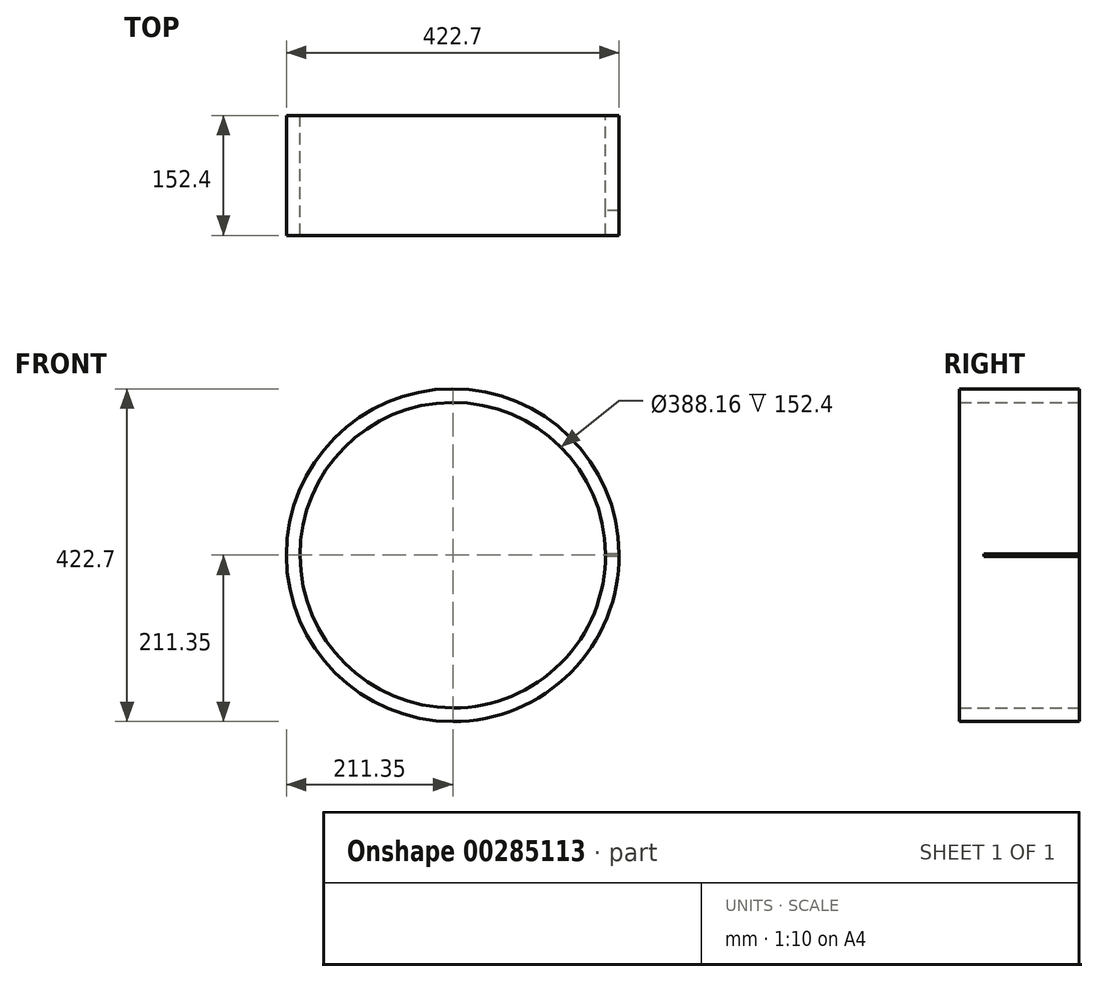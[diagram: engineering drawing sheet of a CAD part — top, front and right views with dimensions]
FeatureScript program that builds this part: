
annotation { "Feature Type Name" : "Feature", "Feature Type Description" : "" }
export const myFeature = defineFeature(function(context is Context, id is Id, definition is map)
    precondition{}
    {
        {
            var Q0;
            Q0=qCreatedBy(makeId("Front.planeOp"),FACE);
            var sketch = newSketch(context, id + "F0", { "sketchPlane" : qUnion([Q0])});
            skCircle(sketch, "E0", {"center": v(0, 0) * mm, "radius": 211.35 * mm});
            skCircle(sketch, "E1", {"center": v(0, 0) * mm, "radius": 194.08 * mm});
            skSolve(sketch);
        }
        {
            var Q0;
            Q0=makeQuery(id+"F0.imprint","IMPRINT",FACE,{"disambiguationData":[TD([[makeQuery(id+"F0.imprint","IMPRINT",EDGE,{"derivedFrom":sQuery(id+"F0.wireOp",EDGE,"E0")}),1.0]])]});
            extrude(context, id + "F1", {"entities" : qUnion([Q0]), "depth" : 152.4 * mm});
        }
        {
            var Q0;
            Q0=qCreatedBy(makeId("Right.planeOp"),FACE);
            var sketch = newSketch(context, id + "F2", { "sketchPlane" : qUnion([Q0])});
            skLineSegment(sketch, "E2.0", {"start": v(0, 1.5) * mm, "end": v(-121, 1.5) * mm});
            skLineSegment(sketch, "E3.0", {"start": v(0, -1.5) * mm, "end": v(-121, -1.5) * mm});
            skLineSegment(sketch, "E4", {"start": v(0, 1.5) * mm, "end": v(0, -1.5) * mm});
            skLineSegment(sketch, "E5", {"start": v(-121, 1.5) * mm, "end": v(-121, -1.5) * mm});
            skSolve(sketch);
        }
        {
            var Q0;
            Q0 = qSketchRegion(id + "F2", true);
            extrude(context, id + "F3", {"entities" : qUnion([Q0]), "operationType" : NewBodyOperationType.REMOVE, "depth" : 253.75 * mm});
        }
    });
